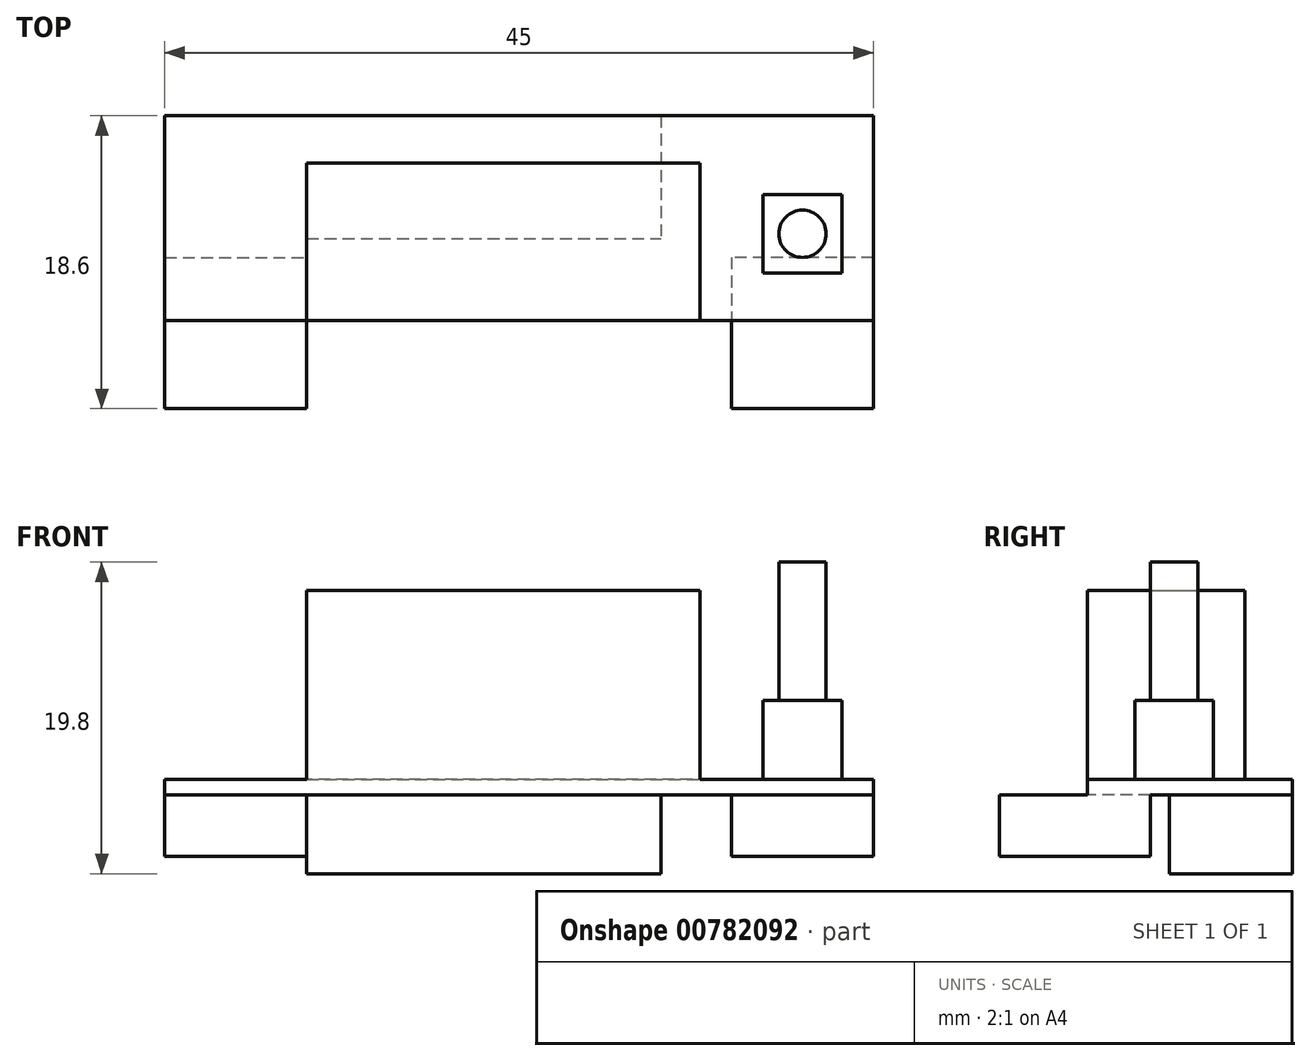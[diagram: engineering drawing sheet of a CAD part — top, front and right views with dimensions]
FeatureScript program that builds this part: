
annotation { "Feature Type Name" : "Feature", "Feature Type Description" : "" }
export const myFeature = defineFeature(function(context is Context, id is Id, definition is map)
    precondition{}
    {
        {
            var Q0;
            Q0=qCreatedBy(makeId("Top.planeOp"),FACE);
            var sketch = newSketch(context, id + "F0", { "sketchPlane" : qUnion([Q0])});
            skLineSegment(sketch, "E0.bottom", {"start": v(0, 0) * mm, "end": v(-45, 0) * mm});
            skLineSegment(sketch, "E0.top", {"start": v(0, 13) * mm, "end": v(-45, 13) * mm});
            skLineSegment(sketch, "E0.left", {"start": v(0, 0) * mm, "end": v(0, 13) * mm});
            skLineSegment(sketch, "E0.right", {"start": v(-45, 0) * mm, "end": v(-45, 13) * mm});
            skSolve(sketch);
        }
        {
            var Q0;
            Q0=makeQuery(id+"F0.imprint","IMPRINT",FACE,{"disambiguationData":[TD([[makeQuery(id+"F0.imprint","IMPRINT",EDGE,{"derivedFrom":sQuery(id+"F0.wireOp",EDGE,"E0.bottom")}),-1.0]])]});
            extrude(context, id + "F1", {"entities" : qUnion([Q0]), "depth" : 1 * mm, "offsetDistance" : 25 * mm});
        }
        {
            var Q0;
            Q0=makeQuery(id+"F1.opExtrude","CAP_FACE",FACE,{"disambiguationData":[OSD([sQuery(id+"F0.wireOp",EDGE,"E0.bottom"),sQuery(id+"F0.wireOp",EDGE,"E0.top"),sQuery(id+"F0.wireOp",EDGE,"E0.left"),sQuery(id+"F0.wireOp",EDGE,"E0.right")])],"isStart":true});
            var sketch = newSketch(context, id + "F2", { "sketchPlane" : qUnion([Q0])});
            skLineSegment(sketch, "E1", {"start": v(-45, -11.2) * mm, "end": v(-36, -11.2) * mm, "construction": true});
            skLineSegment(sketch, "E2.bottom", {"start": v(-36, -13) * mm, "end": v(-13.5, -13) * mm});
            skLineSegment(sketch, "E2.top", {"start": v(-36, -5.2) * mm, "end": v(-13.5, -5.2) * mm});
            skLineSegment(sketch, "E2.left", {"start": v(-36, -13) * mm, "end": v(-36, -5.2) * mm});
            skLineSegment(sketch, "E2.right", {"start": v(-13.5, -13) * mm, "end": v(-13.5, -5.2) * mm});
            skSolve(sketch);
        }
        {
            var Q0;
            Q0=makeQuery(id+"F2.imprint","IMPRINT",FACE,{"disambiguationData":[TD([[makeQuery(id+"F2.imprint","IMPRINT",EDGE,{"derivedFrom":sQuery(id+"F2.wireOp",EDGE,"E2.bottom")}),-1.0]])]});
            extrude(context, id + "F3", {"entities" : qUnion([Q0]), "operationType" : NewBodyOperationType.ADD, "depth" : 5 * mm, "offsetDistance" : 25 * mm});
        }
        {
            var Q0;
            Q0=makeQuery(id+"F1.opExtrude","CAP_FACE",FACE,{"disambiguationData":[OSD([sQuery(id+"F0.wireOp",EDGE,"E0.bottom"),sQuery(id+"F0.wireOp",EDGE,"E0.top"),sQuery(id+"F0.wireOp",EDGE,"E0.left"),sQuery(id+"F0.wireOp",EDGE,"E0.right")])],"isStart":true});
            var sketch = newSketch(context, id + "F4", { "sketchPlane" : qUnion([Q0])});
            skLineSegment(sketch, "E3", {"start": v(-1.97, -13) * mm, "end": v(-1.97, -4) * mm, "construction": true});
            skLineSegment(sketch, "E4.bottom", {"start": v(0, -4) * mm, "end": v(-9, -4) * mm});
            skLineSegment(sketch, "E4.top", {"start": v(0, 5.6) * mm, "end": v(-9, 5.6) * mm});
            skLineSegment(sketch, "E4.left", {"start": v(0, -4) * mm, "end": v(0, 5.6) * mm});
            skLineSegment(sketch, "E4.right", {"start": v(-9, -4) * mm, "end": v(-9, 5.6) * mm});
            skLineSegment(sketch, "E5", {"start": v(-22.5, 0) * mm, "end": v(-22.5, -17.25) * mm, "construction": true});
            skLineSegment(sketch, "E6.MirrorCS", {"start": v(-45, -4) * mm, "end": v(-45, 5.6) * mm});
            skLineSegment(sketch, "E7.MirrorCS", {"start": v(-45, 5.6) * mm, "end": v(-36, 5.6) * mm});
            skLineSegment(sketch, "E8.MirrorCS", {"start": v(-36, -4) * mm, "end": v(-36, 5.6) * mm});
            skLineSegment(sketch, "E9.MirrorCS", {"start": v(-45, -4) * mm, "end": v(-36, -4) * mm});
            skSolve(sketch);
        }
        {
            var Q0;
            {var subQ0=sQuery(id+"F4.wireOp",EDGE,"E4.bottom");Q0=makeQuery(id+"F4.imprint","IMPRINT",FACE,{"disambiguationData":[TD([[makeQuery(id+"F4.imprint","IMPRINT",EDGE,{"derivedFrom":subQ0}),-1.0]])]});}
            var Q1;
            {var subQ0=sQuery(id+"F4.wireOp",EDGE,"E4.top");Q1=makeQuery(id+"F4.imprint","IMPRINT",FACE,{"disambiguationData":[TD([[makeQuery(id+"F4.imprint","IMPRINT",EDGE,{"derivedFrom":subQ0}),1.0]])]});}
            var Q2;
            {var subQ3=sQuery(id+"F4.wireOp",EDGE,"E7.MirrorCS");Q2=makeQuery(id+"F4.imprint","IMPRINT",FACE,{"disambiguationData":[TD([[makeQuery(id+"F4.imprint","IMPRINT",EDGE,{"derivedFrom":subQ3}),-1.0]])]});}
            var Q3;
            {var subQ3=sQuery(id+"F4.wireOp",EDGE,"E9.MirrorCS");Q3=makeQuery(id+"F4.imprint","IMPRINT",FACE,{"disambiguationData":[TD([[makeQuery(id+"F4.imprint","IMPRINT",EDGE,{"derivedFrom":subQ3}),1.0]])]});}
            extrude(context, id + "F5", {"entities" : qUnion([Q0, Q1, Q2, Q3]), "operationType" : NewBodyOperationType.ADD, "depth" : 3.9 * mm, "offsetDistance" : 25 * mm});
        }
        {
            var Q0;
            Q0=makeQuery(id+"F1.opExtrude","CAP_FACE",FACE,{"disambiguationData":[OSD([sQuery(id+"F0.wireOp",EDGE,"E0.bottom"),sQuery(id+"F0.wireOp",EDGE,"E0.top"),sQuery(id+"F0.wireOp",EDGE,"E0.left"),sQuery(id+"F0.wireOp",EDGE,"E0.right")])],"isStart":false});
            var sketch = newSketch(context, id + "F6", { "sketchPlane" : qUnion([Q0])});
            skLineSegment(sketch, "E10", {"start": v(-45, 2.23) * mm, "end": v(-36, 2.23) * mm, "construction": true});
            skLineSegment(sketch, "E11.bottom", {"start": v(-36, 0) * mm, "end": v(-11, 0) * mm});
            skLineSegment(sketch, "E11.top", {"start": v(-36, 10) * mm, "end": v(-11, 10) * mm});
            skLineSegment(sketch, "E11.left", {"start": v(-36, 0) * mm, "end": v(-36, 10) * mm});
            skLineSegment(sketch, "E11.right", {"start": v(-11, 0) * mm, "end": v(-11, 10) * mm});
            skLineSegment(sketch, "E12", {"start": v(-3.26, 13) * mm, "end": v(-3.26, 8) * mm, "construction": true});
            skLineSegment(sketch, "E13", {"start": v(0, 3) * mm, "end": v(-2, 3) * mm, "construction": true});
            skLineSegment(sketch, "E14.bottom", {"start": v(-2, 3) * mm, "end": v(-7, 3) * mm});
            skLineSegment(sketch, "E14.top", {"start": v(-2, 8) * mm, "end": v(-7, 8) * mm});
            skLineSegment(sketch, "E14.left", {"start": v(-2, 3) * mm, "end": v(-2, 8) * mm});
            skLineSegment(sketch, "E14.right", {"start": v(-7, 3) * mm, "end": v(-7, 8) * mm});
            skSolve(sketch);
        }
        {
            var Q0;
            Q0=makeQuery(id+"F6.imprint","IMPRINT",FACE,{"disambiguationData":[TD([[makeQuery(id+"F6.imprint","IMPRINT",EDGE,{"derivedFrom":sQuery(id+"F6.wireOp",EDGE,"E11.bottom")}),-1.0]])]});
            extrude(context, id + "F7", {"entities" : qUnion([Q0]), "operationType" : NewBodyOperationType.ADD, "depth" : 12 * mm, "offsetDistance" : 25 * mm});
        }
        {
            var Q0;
            Q0=makeQuery(id+"F6.imprint","IMPRINT",FACE,{"disambiguationData":[TD([[makeQuery(id+"F6.imprint","IMPRINT",EDGE,{"derivedFrom":sQuery(id+"F6.wireOp",EDGE,"E14.bottom")}),-1.0]])]});
            extrude(context, id + "F8", {"entities" : qUnion([Q0]), "operationType" : NewBodyOperationType.ADD, "depth" : 5 * mm, "offsetDistance" : 25 * mm});
        }
        {
            var Q0;
            Q0=makeQuery(id+"F8.opExtrude","CAP_FACE",FACE,{"disambiguationData":[OSD([sQuery(id+"F6.wireOp",EDGE,"E14.bottom"),sQuery(id+"F6.wireOp",EDGE,"E14.top"),sQuery(id+"F6.wireOp",EDGE,"E14.left"),sQuery(id+"F6.wireOp",EDGE,"E14.right")])],"isStart":false});
            var sketch = newSketch(context, id + "F9", { "sketchPlane" : qUnion([Q0])});
            skLineSegment(sketch, "E15", {"start": v(-7, 8) * mm, "end": v(-2, 3) * mm, "construction": true});
            skLineSegment(sketch, "E16", {"start": v(-2, 8) * mm, "end": v(-7, 3) * mm, "construction": true});
            skCircle(sketch, "E17", {"center": v(-4.5, 5.5) * mm, "radius": 1.5 * mm});
            skSolve(sketch);
        }
        {
            var Q0;
            Q0 = qSketchRegion(id + "F9", true);
            extrude(context, id + "F10", {"entities" : qUnion([Q0]), "operationType" : NewBodyOperationType.ADD, "depth" : 8.8 * mm, "offsetDistance" : 25 * mm});
        }
    });
